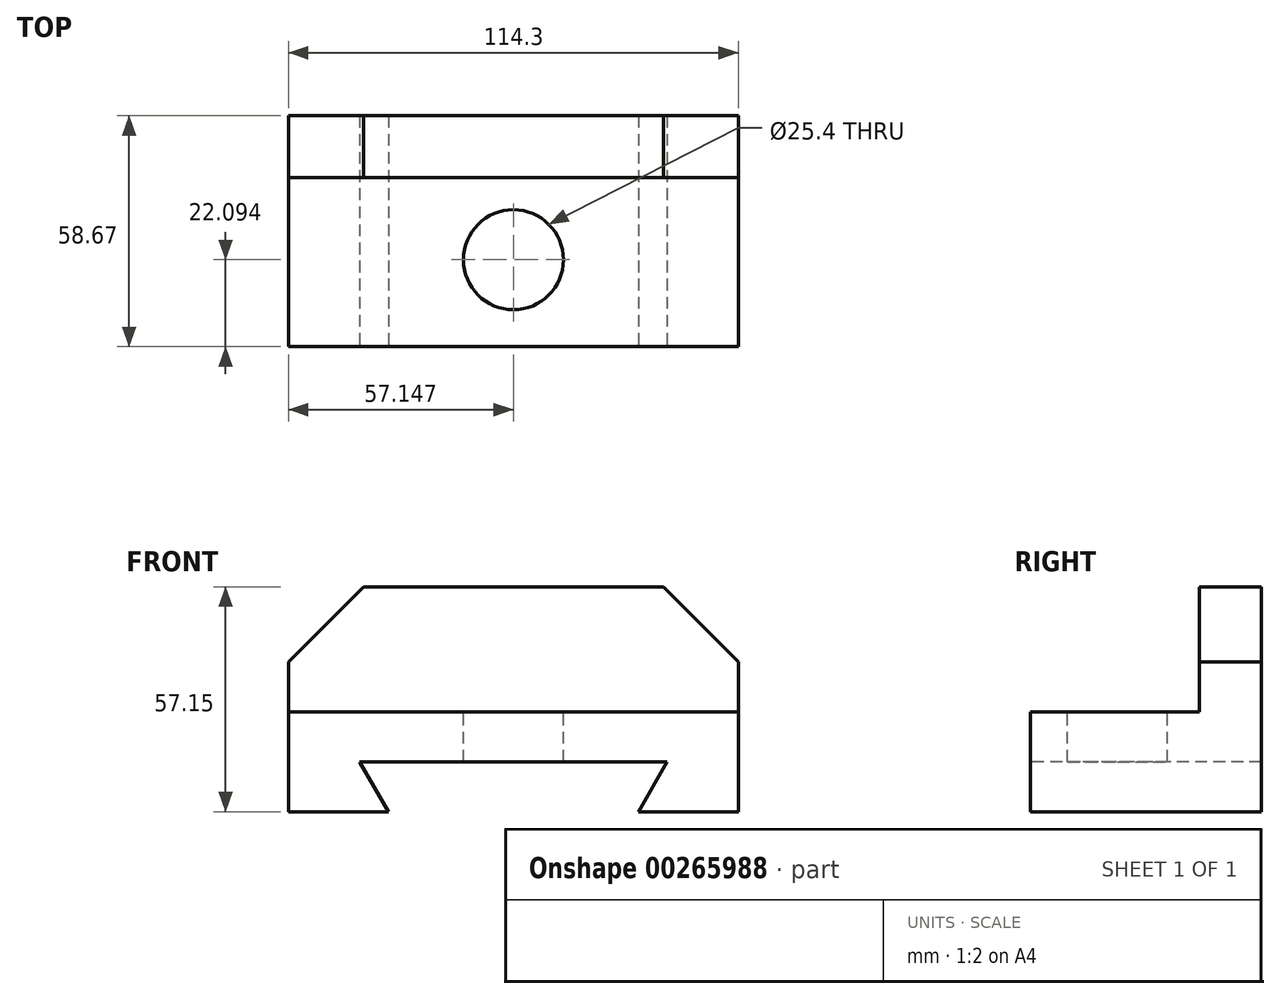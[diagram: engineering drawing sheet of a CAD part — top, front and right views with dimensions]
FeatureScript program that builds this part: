
annotation { "Feature Type Name" : "Feature", "Feature Type Description" : "" }
export const myFeature = defineFeature(function(context is Context, id is Id, definition is map)
    precondition{}
    {
        {
            var Q0;
            Q0=qCreatedBy(makeId("Front.planeOp"),FACE);
            var sketch = newSketch(context, id + "F0", { "sketchPlane" : qUnion([Q0])});
            skLineSegment(sketch, "E0.bottom", {"start": v(-63.36, 19.24) * mm, "end": v(50.94, 19.24) * mm});
            skLineSegment(sketch, "E0.top", {"start": v(-63.36, -37.91) * mm, "end": v(50.94, -37.91) * mm});
            skLineSegment(sketch, "E0.left", {"start": v(-63.36, 19.24) * mm, "end": v(-63.36, -37.91) * mm});
            skLineSegment(sketch, "E0.right", {"start": v(50.94, 19.24) * mm, "end": v(50.94, -37.91) * mm});
            skSolve(sketch);
        }
        {
            var Q0;
            Q0 = qSketchRegion(id + "F0", true);
            extrude(context, id + "F1", {"entities" : qUnion([Q0]), "depth" : 58.67 * mm});
        }
        {
            var Q0;
            Q0=makeQuery(id+"F1.opExtrude","SWEPT_FACE",FACE,{"disambiguationData":[OSD([sQuery(id+"F0.wireOp",EDGE,"E0.bottom")])]});
            var sketch = newSketch(context, id + "F2", { "sketchPlane" : qUnion([Q0])});
            skLineSegment(sketch, "E1.bottom", {"start": v(-63.36, -15.75) * mm, "end": v(50.94, -15.75) * mm});
            skLineSegment(sketch, "E1.top", {"start": v(-63.36, -58.67) * mm, "end": v(50.94, -58.67) * mm});
            skLineSegment(sketch, "E1.left", {"start": v(-63.36, -15.75) * mm, "end": v(-63.36, -58.67) * mm});
            skLineSegment(sketch, "E1.right", {"start": v(50.94, -15.75) * mm, "end": v(50.94, -58.67) * mm});
            skSolve(sketch);
        }
        {
            var Q0;
            Q0=makeQuery(id+"F2.imprint","IMPRINT",FACE,{"disambiguationData":[TD([[makeQuery(id+"F2.imprint","IMPRINT",EDGE,{"derivedFrom":sQuery(id+"F2.wireOp",EDGE,"E1.bottom")}),-1.0]])]});
            extrude(context, id + "F3", {"entities" : qUnion([Q0]), "operationType" : NewBodyOperationType.REMOVE, "oppositeDirection" : true, "depth" : 31.75 * mm});
        }
        {
            var Q0;
            Q0=makeQuery(id+"F3.boolean.opBoolean","COPY",FACE,{"derivedFrom":makeQuery(id+"F3.opExtrude","SWEPT_FACE",FACE,{"disambiguationData":[OSD([sQuery(id+"F2.wireOp",EDGE,"E1.bottom")])]})});
            var sketch = newSketch(context, id + "F4", { "sketchPlane" : qUnion([Q0])});
            skLineSegment(sketch, "E2", {"start": v(-63.36, 19.24) * mm, "end": v(-44.31, 19.24) * mm});
            skLineSegment(sketch, "E3", {"start": v(-63.36, 19.24) * mm, "end": v(-63.36, 0.19) * mm});
            skLineSegment(sketch, "E4", {"start": v(50.94, 19.24) * mm, "end": v(31.89, 19.24) * mm});
            skLineSegment(sketch, "E5", {"start": v(50.94, 19.24) * mm, "end": v(50.94, 0.19) * mm});
            skLineSegment(sketch, "E6", {"start": v(-63.36, 0.19) * mm, "end": v(-44.31, 19.24) * mm});
            skLineSegment(sketch, "E7", {"start": v(31.89, 19.24) * mm, "end": v(50.94, 0.19) * mm});
            skSolve(sketch);
        }
        {
            var Q0;
            Q0=makeQuery(id+"F4.imprint","IMPRINT",FACE,{"disambiguationData":[TD([[makeQuery(id+"F4.imprint","IMPRINT",EDGE,{"derivedFrom":sQuery(id+"F4.wireOp",EDGE,"E4")}),-1.0]])]});
            var Q1;
            Q1=makeQuery(id+"F4.imprint","IMPRINT",FACE,{"disambiguationData":[TD([[makeQuery(id+"F4.imprint","IMPRINT",EDGE,{"derivedFrom":sQuery(id+"F4.wireOp",EDGE,"E2")}),-1.0]])]});
            extrude(context, id + "F5", {"entities" : qUnion([Q0, Q1]), "operationType" : NewBodyOperationType.REMOVE, "oppositeDirection" : true, "depth" : 15.75 * mm});
        }
        {
            var Q0;
            Q0=makeQuery(id+"F1.opExtrude","CAP_FACE",FACE,{"disambiguationData":[OSD([sQuery(id+"F0.wireOp",EDGE,"E0.bottom"),sQuery(id+"F0.wireOp",EDGE,"E0.top"),sQuery(id+"F0.wireOp",EDGE,"E0.left"),sQuery(id+"F0.wireOp",EDGE,"E0.right")])],"isStart":false});
            var sketch = newSketch(context, id + "F6", { "sketchPlane" : qUnion([Q0])});
            skLineSegment(sketch, "E8", {"start": v(50.94, -37.91) * mm, "end": v(25.54, -37.91) * mm});
            skLineSegment(sketch, "E9", {"start": v(25.54, -37.91) * mm, "end": v(-37.96, -37.91) * mm});
            skLineSegment(sketch, "E10", {"start": v(-63.36, -37.91) * mm, "end": v(-37.96, -37.91) * mm});
            skLineSegment(sketch, "E11", {"start": v(-37.96, -25.21) * mm, "end": v(-45.3, -25.21) * mm});
            skLineSegment(sketch, "E12", {"start": v(-45.3, -25.21) * mm, "end": v(-37.96, -37.91) * mm});
            skLineSegment(sketch, "E13", {"start": v(25.54, -25.21) * mm, "end": v(32.87, -25.21) * mm});
            skLineSegment(sketch, "E14", {"start": v(32.87, -25.21) * mm, "end": v(25.54, -37.91) * mm});
            skLineSegment(sketch, "E15", {"start": v(-45.3, -25.21) * mm, "end": v(32.87, -25.21) * mm});
            skLineSegment(sketch, "E16", {"start": v(-37.96, -37.91) * mm, "end": v(25.54, -37.91) * mm});
            skSolve(sketch);
        }
        {
            var Q0;
            {var subQ3=sQuery(id+"F6.wireOp",EDGE,"E12");Q0=makeQuery(id+"F6.imprint","IMPRINT",FACE,{"disambiguationData":[TD([[makeQuery(id+"F6.imprint","IMPRINT",EDGE,{"derivedFrom":subQ3}),1.0]])]});}
            extrude(context, id + "F7", {"entities" : qUnion([Q0]), "operationType" : NewBodyOperationType.REMOVE, "oppositeDirection" : true, "depth" : 58.67 * mm});
        }
        {
            var Q0;
            Q0=makeQuery(id+"F3.boolean.opBoolean","COPY",FACE,{"derivedFrom":makeQuery(id+"F3.opExtrude","CAP_FACE",FACE,{"disambiguationData":[OSD([sQuery(id+"F2.wireOp",EDGE,"E1.bottom"),sQuery(id+"F2.wireOp",EDGE,"E1.top"),sQuery(id+"F2.wireOp",EDGE,"E1.left"),sQuery(id+"F2.wireOp",EDGE,"E1.right")])],"isStart":false})});
            var sketch = newSketch(context, id + "F8", { "sketchPlane" : qUnion([Q0])});
            skLineSegment(sketch, "E17", {"start": v(50.94, -58.67) * mm, "end": v(-6.21, -58.67) * mm});
            skLineSegment(sketch, "E18", {"start": v(-6.21, -58.67) * mm, "end": v(50.94, -58.67) * mm});
            skLineSegment(sketch, "E19", {"start": v(-6.21, -58.67) * mm, "end": v(-6.21, -36.58) * mm});
            skCircle(sketch, "E20", {"center": v(-6.21, -36.58) * mm, "radius": 12.7 * mm});
            skSolve(sketch);
        }
        {
            var Q0;
            Q0=makeQuery(id+"F8.imprint","IMPRINT",FACE,{"disambiguationData":[TD([[makeQuery(id+"F8.imprint","IMPRINT",EDGE,{"derivedFrom":sQuery(id+"F8.wireOp",EDGE,"E20")}),1.0]])]});
            extrude(context, id + "F9", {"entities" : qUnion([Q0]), "operationType" : NewBodyOperationType.REMOVE, "oppositeDirection" : true, "depth" : 12.7 * mm});
        }
    });
